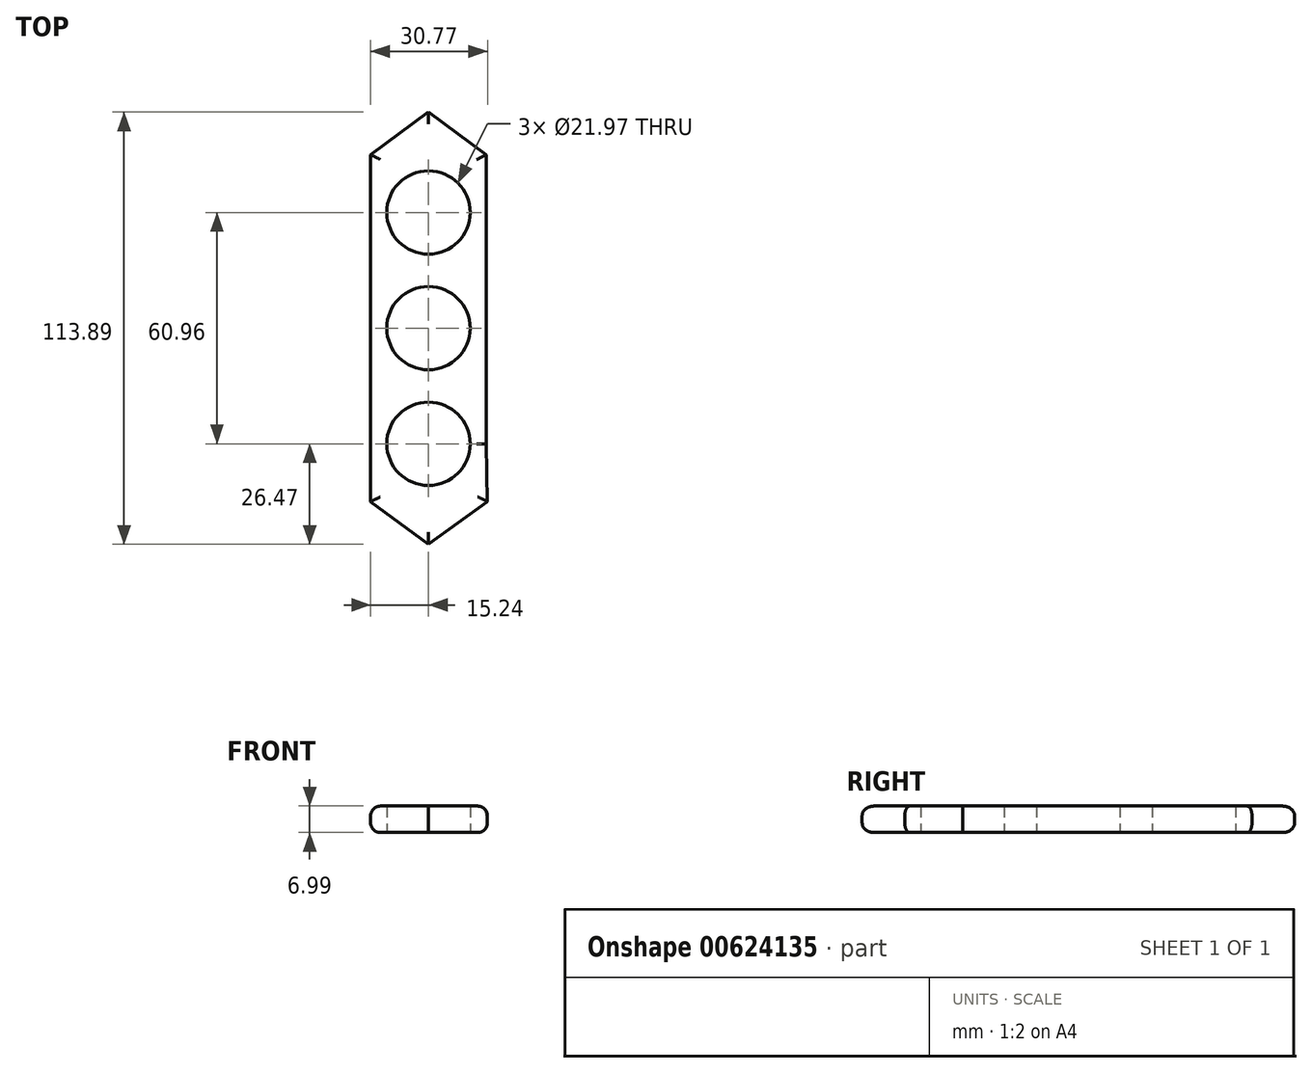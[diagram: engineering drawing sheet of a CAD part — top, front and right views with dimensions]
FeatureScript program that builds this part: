
annotation { "Feature Type Name" : "Feature", "Feature Type Description" : "" }
export const myFeature = defineFeature(function(context is Context, id is Id, definition is map)
    precondition{}
    {
        {
            var Q0;
            Q0=qCreatedBy(makeId("Top.planeOp"),FACE);
            var sketch = newSketch(context, id + "F0", { "sketchPlane" : qUnion([Q0])});
            skCircle(sketch, "E0", {"center": v(0, 0) * mm, "radius": 10.99 * mm});
            skCircle(sketch, "E1", {"center": v(0, 0) * mm, "radius": 15.24 * mm});
            skLineSegment(sketch, "E2", {"start": v(0, 0) * mm, "end": v(0, 30.48) * mm});
            skLineSegment(sketch, "E3", {"start": v(0, 0) * mm, "end": v(0, -30.48) * mm});
            skCircle(sketch, "E4", {"center": v(0, 30.48) * mm, "radius": 10.99 * mm});
            skCircle(sketch, "E5", {"center": v(0, 30.48) * mm, "radius": 15.24 * mm});
            skCircle(sketch, "E6", {"center": v(0, -30.48) * mm, "radius": 10.99 * mm});
            skCircle(sketch, "E7", {"center": v(0, -30.48) * mm, "radius": 15.24 * mm});
            skLineSegment(sketch, "E8", {"start": v(-15.24, 30.48) * mm, "end": v(-15.24, 0) * mm});
            skLineSegment(sketch, "E9", {"start": v(15.24, 30.48) * mm, "end": v(15.24, 0) * mm});
            skLineSegment(sketch, "E10", {"start": v(-15.24, 0) * mm, "end": v(-15.24, -30.48) * mm});
            skLineSegment(sketch, "E11", {"start": v(15.24, 0) * mm, "end": v(15.24, -30.48) * mm});
            skLineSegment(sketch, "E12", {"start": v(-15.24, 30.48) * mm, "end": v(-15.24, 45.72) * mm});
            skLineSegment(sketch, "E13", {"start": v(-15.24, 45.72) * mm, "end": v(15.24, 45.72) * mm});
            skLineSegment(sketch, "E14", {"start": v(15.24, 45.72) * mm, "end": v(15.24, 30.48) * mm});
            skLineSegment(sketch, "E15", {"start": v(-15.24, -45.72) * mm, "end": v(15.53, -45.72) * mm});
            skLineSegment(sketch, "E16", {"start": v(15.53, -45.72) * mm, "end": v(15.24, -30.48) * mm});
            skLineSegment(sketch, "E17", {"start": v(-15.24, -30.48) * mm, "end": v(-15.24, -45.72) * mm});
            skLineSegment(sketch, "E18", {"start": v(-15.24, -45.72) * mm, "end": v(0, -56.95) * mm});
            skLineSegment(sketch, "E19", {"start": v(15.53, -45.72) * mm, "end": v(0, -56.95) * mm});
            skLineSegment(sketch, "E20", {"start": v(-15.24, 45.72) * mm, "end": v(0, 56.94) * mm});
            skLineSegment(sketch, "E21", {"start": v(15.24, 45.72) * mm, "end": v(0, 56.94) * mm});
            skSolve(sketch);
        }
        {
            var Q0;
            {var subQ0=sQuery(id+"F0.wireOp",EDGE,"E8");Q0=makeQuery(id+"F0.imprint","IMPRINT",FACE,{"disambiguationData":[TD([[makeQuery(id+"F0.imprint","IMPRINT",EDGE,{"derivedFrom":subQ0}),1.0]])]});}
            var Q1;
            {var subQ0=sQuery(id+"F0.wireOp",EDGE,"E9");Q1=makeQuery(id+"F0.imprint","IMPRINT",FACE,{"disambiguationData":[TD([[makeQuery(id+"F0.imprint","IMPRINT",EDGE,{"derivedFrom":subQ0}),-1.0]])]});}
            var Q2;
            {var subQ0=sQuery(id+"F0.wireOp",EDGE,"E12");Q2=makeQuery(id+"F0.imprint","IMPRINT",FACE,{"disambiguationData":[TD([[makeQuery(id+"F0.imprint","IMPRINT",EDGE,{"derivedFrom":subQ0}),-1.0]])]});}
            var Q3;
            {var subQ0=sQuery(id+"F0.wireOp",EDGE,"E14");Q3=makeQuery(id+"F0.imprint","IMPRINT",FACE,{"disambiguationData":[TD([[makeQuery(id+"F0.imprint","IMPRINT",EDGE,{"derivedFrom":subQ0}),-1.0]])]});}
            var Q4;
            {var subQ0=sQuery(id+"F0.wireOp",EDGE,"E20");Q4=makeQuery(id+"F0.imprint","IMPRINT",FACE,{"disambiguationData":[TD([[makeQuery(id+"F0.imprint","IMPRINT",EDGE,{"derivedFrom":subQ0}),-1.0]])]});}
            var Q5;
            Q5=makeQuery(id+"F0.imprint","IMPRINT",FACE,{"disambiguationData":[TD([[makeQuery(id+"F0.imprint","IMPRINT",EDGE,{"derivedFrom":sQuery(id+"F0.wireOp",EDGE,"E4")}),-1.0]])]});
            var Q6;
            {var subQ4=sQuery(id+"F0.wireOp",EDGE,"E2");var subQ5=sQuery(id+"F0.wireOp",EDGE,"E0");var subQ6=makeQuery(id+"F0.imprint","INTERSECT",VERTEX,{"derivedFrom":[subQ5,subQ4]});Q6=makeQuery(id+"F0.imprint","IMPRINT",FACE,{"disambiguationData":[TD([[makeQuery(id+"F0.imprint","IMPRINT",EDGE,{"disambiguationData":[TD([[subQ6,1.0]])],"derivedFrom":subQ5}),-1.0]])]});}
            var Q7;
            {var subQ0=sQuery(id+"F0.wireOp",EDGE,"E10");Q7=makeQuery(id+"F0.imprint","IMPRINT",FACE,{"disambiguationData":[TD([[makeQuery(id+"F0.imprint","IMPRINT",EDGE,{"derivedFrom":subQ0}),1.0]])]});}
            var Q8;
            {var subQ0=sQuery(id+"F0.wireOp",EDGE,"E2");var subQ1=sQuery(id+"F0.wireOp",EDGE,"E0");var subQ2=makeQuery(id+"F0.imprint","INTERSECT",VERTEX,{"derivedFrom":[subQ1,subQ0]});Q8=makeQuery(id+"F0.imprint","IMPRINT",FACE,{"disambiguationData":[TD([[makeQuery(id+"F0.imprint","IMPRINT",EDGE,{"disambiguationData":[TD([[subQ2,-1.0]])],"derivedFrom":subQ1}),-1.0]])]});}
            var Q9;
            {var subQ0=sQuery(id+"F0.wireOp",EDGE,"E11");Q9=makeQuery(id+"F0.imprint","IMPRINT",FACE,{"disambiguationData":[TD([[makeQuery(id+"F0.imprint","IMPRINT",EDGE,{"derivedFrom":subQ0}),-1.0]])]});}
            var Q10;
            Q10=makeQuery(id+"F0.imprint","IMPRINT",FACE,{"disambiguationData":[TD([[makeQuery(id+"F0.imprint","IMPRINT",EDGE,{"derivedFrom":sQuery(id+"F0.wireOp",EDGE,"E6")}),-1.0]])]});
            var Q11;
            {var subQ0=sQuery(id+"F0.wireOp",EDGE,"E17");var subQ1=sQuery(id+"F0.wireOp",EDGE,"E7");var subQ2=makeQuery(id+"F0.imprint","INTERSECT",VERTEX,{"derivedFrom":[subQ1,subQ0]});Q11=makeQuery(id+"F0.imprint","IMPRINT",FACE,{"disambiguationData":[TD([[makeQuery(id+"F0.imprint","IMPRINT",EDGE,{"disambiguationData":[TD([[subQ2,-1.0]])],"derivedFrom":subQ1}),-1.0]])]});}
            var Q12;
            {var subQ0=sQuery(id+"F0.wireOp",EDGE,"E16");Q12=makeQuery(id+"F0.imprint","IMPRINT",FACE,{"disambiguationData":[TD([[makeQuery(id+"F0.imprint","IMPRINT",EDGE,{"derivedFrom":subQ0}),1.0]])]});}
            var Q13;
            {var subQ0=sQuery(id+"F0.wireOp",EDGE,"E18");Q13=makeQuery(id+"F0.imprint","IMPRINT",FACE,{"disambiguationData":[TD([[makeQuery(id+"F0.imprint","IMPRINT",EDGE,{"derivedFrom":subQ0}),1.0]])]});}
            extrude(context, id + "F1", {"entities" : qUnion([Q0, Q1, Q2, Q3, Q4, Q5, Q6, Q7, Q8, Q9, Q10, Q11, Q12, Q13]), "depth" : 7 * mm, "offsetDistance" : 25.4 * mm});
        }
        {
            var Q0;
            Q0=makeQuery(id+"F1.opExtrude","CAP_EDGE",EDGE,{"disambiguationData":[OSD([sQuery(id+"F0.wireOp",EDGE,"E8"),sQuery(id+"F0.wireOp",EDGE,"E10"),sQuery(id+"F0.wireOp",EDGE,"E12")])],"isStart":false});
            var Q1;
            Q1=makeQuery(id+"F1.opExtrude","CAP_EDGE",EDGE,{"disambiguationData":[OSD([sQuery(id+"F0.wireOp",EDGE,"E9"),sQuery(id+"F0.wireOp",EDGE,"E11")])],"isStart":false});
            var Q2;
            Q2=makeQuery(id+"F1.opExtrude","CAP_EDGE",EDGE,{"disambiguationData":[OSD([sQuery(id+"F0.wireOp",EDGE,"E21")])],"isStart":false});
            var Q3;
            Q3=makeQuery(id+"F1.opExtrude","CAP_EDGE",EDGE,{"disambiguationData":[OSD([sQuery(id+"F0.wireOp",EDGE,"E20")])],"isStart":false});
            var Q4;
            Q4=makeQuery(id+"F1.opExtrude","CAP_EDGE",EDGE,{"disambiguationData":[OSD([sQuery(id+"F0.wireOp",EDGE,"E18")])],"isStart":false});
            var Q5;
            Q5=makeQuery(id+"F1.opExtrude","CAP_EDGE",EDGE,{"disambiguationData":[OSD([sQuery(id+"F0.wireOp",EDGE,"E19")])],"isStart":false});
            var Q6;
            Q6=makeQuery(id+"F1.opExtrude","CAP_EDGE",EDGE,{"disambiguationData":[OSD([sQuery(id+"F0.wireOp",EDGE,"E17")])],"isStart":false});
            var Q7;
            Q7=makeQuery(id+"F1.opExtrude","CAP_EDGE",EDGE,{"disambiguationData":[OSD([sQuery(id+"F0.wireOp",EDGE,"E16")])],"isStart":false});
            var Q8;
            Q8=makeQuery(id+"F1.opExtrude","CAP_EDGE",EDGE,{"disambiguationData":[OSD([sQuery(id+"F0.wireOp",EDGE,"E14")])],"isStart":false});
            fillet(context, id + "F2", {"entities" : qUnion([Q0, Q1, Q2, Q3, Q4, Q5, Q6, Q7, Q8]), "radius" : 2.54 * mm, "tangentPropagation" : true, "allowEdgeOverflow" : false});
        }
        {
            var Q0;
            Q0=makeQuery(id+"F1.opExtrude","CAP_EDGE",EDGE,{"disambiguationData":[OSD([sQuery(id+"F0.wireOp",EDGE,"E14")])],"isStart":true});
            var Q1;
            Q1=makeQuery(id+"F1.opExtrude","CAP_EDGE",EDGE,{"disambiguationData":[OSD([sQuery(id+"F0.wireOp",EDGE,"E9"),sQuery(id+"F0.wireOp",EDGE,"E11")])],"isStart":true});
            var Q2;
            Q2=makeQuery(id+"F1.opExtrude","CAP_EDGE",EDGE,{"disambiguationData":[OSD([sQuery(id+"F0.wireOp",EDGE,"E16")])],"isStart":true});
            var Q3;
            Q3=makeQuery(id+"F1.opExtrude","CAP_EDGE",EDGE,{"disambiguationData":[OSD([sQuery(id+"F0.wireOp",EDGE,"E19")])],"isStart":true});
            var Q4;
            Q4=makeQuery(id+"F1.opExtrude","CAP_EDGE",EDGE,{"disambiguationData":[OSD([sQuery(id+"F0.wireOp",EDGE,"E18")])],"isStart":true});
            var Q5;
            Q5=makeQuery(id+"F1.opExtrude","CAP_EDGE",EDGE,{"disambiguationData":[OSD([sQuery(id+"F0.wireOp",EDGE,"E8"),sQuery(id+"F0.wireOp",EDGE,"E10"),sQuery(id+"F0.wireOp",EDGE,"E12")])],"isStart":true});
            var Q6;
            Q6=makeQuery(id+"F1.opExtrude","CAP_EDGE",EDGE,{"disambiguationData":[OSD([sQuery(id+"F0.wireOp",EDGE,"E17")])],"isStart":true});
            var Q7;
            Q7=makeQuery(id+"F1.opExtrude","CAP_EDGE",EDGE,{"disambiguationData":[OSD([sQuery(id+"F0.wireOp",EDGE,"E20")])],"isStart":true});
            var Q8;
            Q8=makeQuery(id+"F1.opExtrude","CAP_EDGE",EDGE,{"disambiguationData":[OSD([sQuery(id+"F0.wireOp",EDGE,"E21")])],"isStart":true});
            fillet(context, id + "F3", {"entities" : qUnion([Q0, Q1, Q2, Q3, Q4, Q5, Q6, Q7, Q8]), "radius" : 2.54 * mm, "tangentPropagation" : true, "allowEdgeOverflow" : false});
        }
    });
